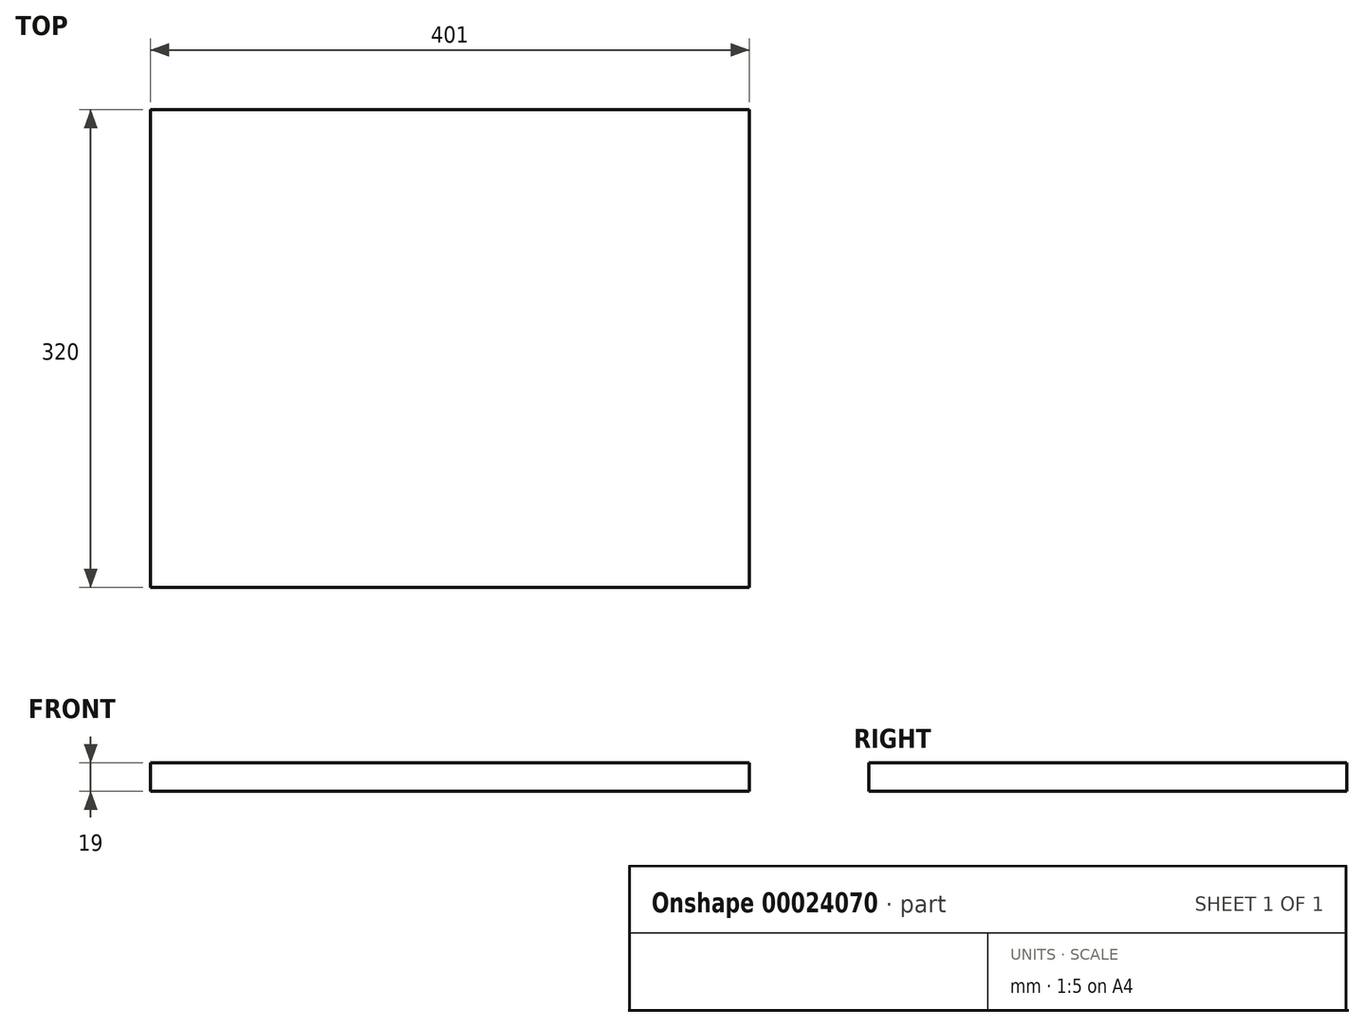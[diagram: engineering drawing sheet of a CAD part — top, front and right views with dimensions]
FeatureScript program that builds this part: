
annotation { "Feature Type Name" : "Feature", "Feature Type Description" : "" }
export const myFeature = defineFeature(function(context is Context, id is Id, definition is map)
    precondition{}
    {
        {
            var Q0;
            Q0=qCreatedBy(makeId("Top.planeOp"),FACE);
            var sketch = newSketch(context, id + "F0", { "sketchPlane" : qUnion([Q0])});
            skLineSegment(sketch, "E0.bottom", {"start": v(-70.96, 65.05) * mm, "end": v(330.04, 65.05) * mm});
            skLineSegment(sketch, "E0.top", {"start": v(-70.96, -254.95) * mm, "end": v(330.04, -254.95) * mm});
            skLineSegment(sketch, "E0.left", {"start": v(-70.96, 65.05) * mm, "end": v(-70.96, -254.95) * mm});
            skLineSegment(sketch, "E0.right", {"start": v(330.04, 65.05) * mm, "end": v(330.04, -254.95) * mm});
            skSolve(sketch);
        }
        {
            var Q0;
            Q0=qSketchRegion(id+"F0",true);
            extrude(context, id + "F1", {"entities" : qUnion([Q0]), "depth" : 19 * mm});
        }
    });
